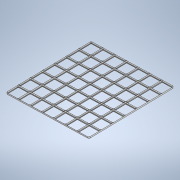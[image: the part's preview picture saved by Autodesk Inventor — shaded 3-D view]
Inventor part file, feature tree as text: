
AUTODESK INVENTOR PART (.ipt)
format: ipt  version: 2022.3 (Build 263350000, 350)  size: 1,134,592 bytes
history: native  units: mm
features: sketch x4, extrude x3, plane x1, sweep x1, boolean_combine x1, thicken_offset x1, pattern_linear x1, projected_geometry x1
ambient origin geometry x8: Origin, YZ Plane, XZ Plane, XY Plane, X Axis, Y Axis, Z Axis, Center Point
bodies: Solid1 (feature_tree), Solid2 (feature_tree)
feature tree (13):
  sketch  "Sketch1"  dims[d0=42.0mm d1=42.0mm]
  extrude  "Extrusion1"  Depth=42.0mm
  plane  "Work Plane1"
  sweep  "Sweep1"
  extrude  "Extrusion2"  Depth=2.4mm
  boolean_combine  "Combine1"
  thicken_offset  "Thicken1"
  pattern_linear  "Rectangular Pattern1"  Spacing1=0.8mm  [1 undecoded]
  extrude  "Extrusion3"  Depth=4.0mm
  sketch  "Sketch2"  dims[d6=5.0mm d7=0.0mm]
  projected_geometry  "Projected Loop1"
  sketch  "Sketch3"  dims[d8=45.0deg d9=2.4mm]
  sketch  "Sketch4"  dims[d10=45.0deg d11=0.8mm d12=4.0mm d13=0.0mm d14=0.0mm d15=5.0mm d16=0.0mm d17=0.25mm d18=0.25mm d19=70.0mm d21=42.0mm d22=70.0mm d24=42.0mm d25=0.0mm d26=0.0mm d27=147.0mm d28=147.0mm d29=4.0mm]
note: 1 required parameter value undecoded (feature->parameter linkage not recoverable at this tier; creation-order binding heuristic only, values carry confidence <= 0.55)
